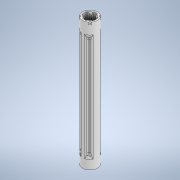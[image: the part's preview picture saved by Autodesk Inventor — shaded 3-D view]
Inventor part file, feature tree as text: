
AUTODESK INVENTOR PART (.ipt)
format: ipt  version: 2022 (Build 260153000, 153)  size: 485,376 bytes
history: native  units: in
note: dims shown in document units (in); Inventor stores cm internally (conversion verified against a paired STEP export)
features: sketch x7, extrude x6, fillet x2, mirror x2, chamfer x1, plane x1, revolve x1
ambient origin geometry x8: Origin, YZ Plane, XZ Plane, XY Plane, X Axis, Y Axis, Z Axis, Center Point
bodies: Solid1 (feature_tree)
feature tree (20):
  extrude  "Extrusion1"  Depth=5.0394in TaperAngle=0.0deg
  extrude  "Extrusion2"  Depth=0.7087in
  extrude  "Extrusion3"  Depth=0.315in TaperAngle=0.0deg
  extrude  "Extrusion6"  Depth=0.0394in
  extrude  "Extrusion7"  Depth=0.0394in
  extrude  "Extrusion14"  Depth=0.1949in
  chamfer  "Chamfer1"  Distance=1.5748in Angle=360.0deg
  plane  "Work Plane1"
  revolve  "Revolution1"  [1 undecoded]
  fillet  "Fillet3"  Radius=0.3898in
  fillet  "Fillet4"  Radius=0.2126in
  mirror  "Mirror1"
  mirror  "Mirror2"
  sketch  "Sketch1"  dims[d0=0.5512in d1=5.0394in d2=0.0in]
  sketch  "Sketch2"  dims[d13=0.0in d14=0.0in d15=0.7087in]
  sketch  "Sketch3"  dims[d19=0.3543in d20=0.315in d21=0.0in]
  sketch  "Sketch6"  dims[d36=0.0394in d37=0.0394in]
  sketch  "Sketch7"  dims[d38=0.0394in d39=0.0394in]
  sketch  "Sketch12"  dims[d69=0.0787in d70=0.1949in]
  sketch  "Sketch13"  dims[d71=0.1949in d72=1.5748in d74=360.0deg d76=0.0787in d77=0.0in d78=0.3898in d79=0.2126in d80=0.0in d81=0.0in d93=0.3071in d94=0.1339in d95=0.122in d97=1.5748in d99=360.0deg d120=0.1535in d121=0.122in d128=0.7874in d129=0.0in d130=0.0394in d131=0.0787in d132=60.0deg d133=45.0deg d134=3.8583in d135=0.0591in d136=0.3937in d137=0.1374in d138=0.0344in d139=0.1575in d140=0.0472in d67=0.0197in d68=0.0344in d91=0.0197in d92=0.0344in d109=0.0197in d110=0.0344in d111=0.0197in d112=0.0344in]
note: 1 required parameter value undecoded (feature->parameter linkage not recoverable at this tier; creation-order binding heuristic only, values carry confidence <= 0.55)
